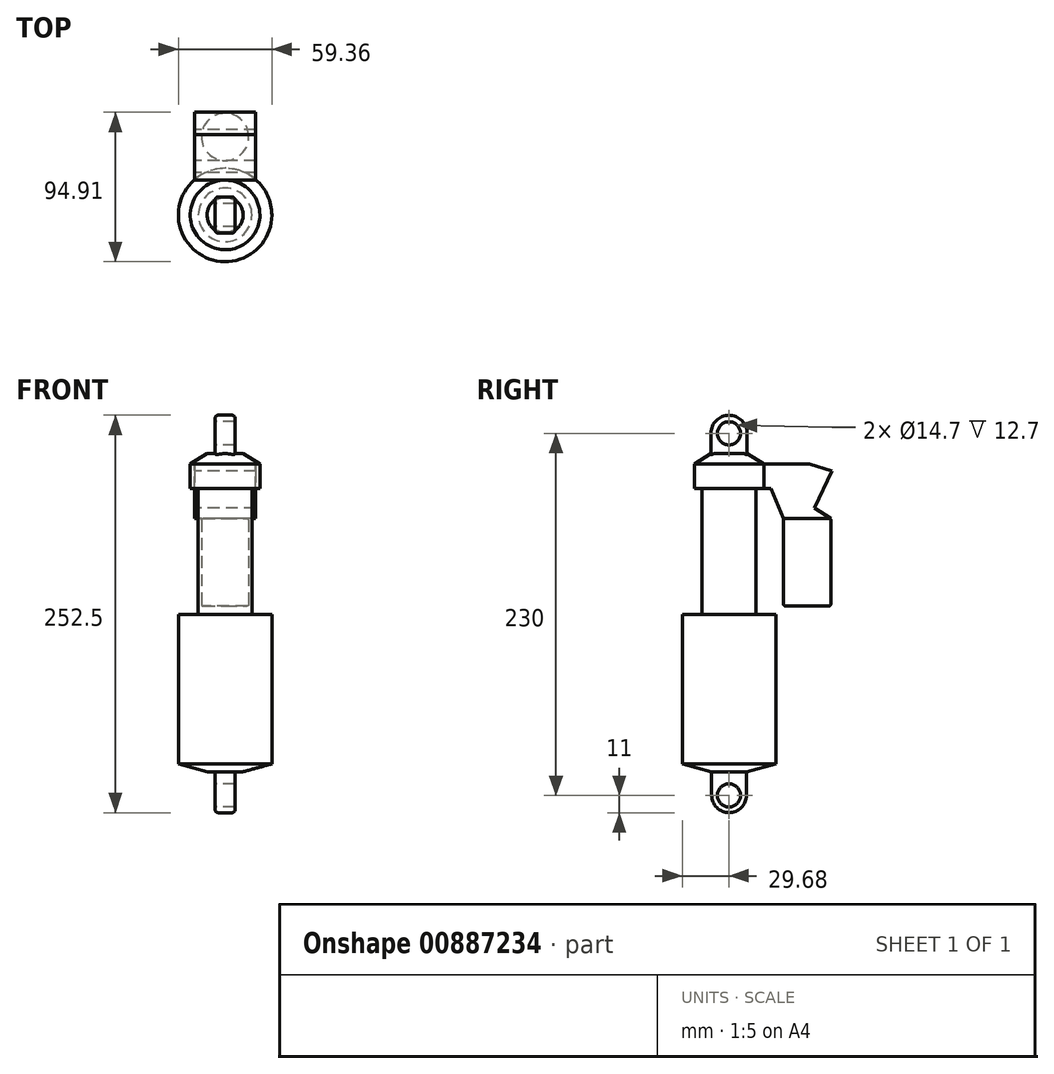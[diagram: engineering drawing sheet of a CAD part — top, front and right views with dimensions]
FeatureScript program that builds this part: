
annotation { "Feature Type Name" : "Feature", "Feature Type Description" : "" }
export const myFeature = defineFeature(function(context is Context, id is Id, definition is map)
    precondition{}
    {
        {
            var Q0;
            Q0=qCreatedBy(makeId("Right.planeOp"),FACE);
            var sketch = newSketch(context, id + "F0", { "sketchPlane" : qUnion([Q0])});
            skCircle(sketch, "E0", {"center": v(0, 0) * mm, "radius": 7.35 * mm});
            skCircle(sketch, "E1", {"center": v(0, 0) * mm, "radius": 11 * mm});
            skCircle(sketch, "E2", {"center": v(0, 230) * mm, "radius": 7.35 * mm});
            skCircle(sketch, "E3", {"center": v(0, 230) * mm, "radius": 11.5 * mm});
            skLineSegment(sketch, "E4.bottom", {"start": v(29.67, 20) * mm, "end": v(-29.68, 20) * mm});
            skLineSegment(sketch, "E4.top", {"start": v(29.67, 115) * mm, "end": v(-29.68, 115) * mm});
            skLineSegment(sketch, "E4.left", {"start": v(29.67, 20) * mm, "end": v(29.67, 115) * mm});
            skLineSegment(sketch, "E4.right", {"start": v(-29.68, 20) * mm, "end": v(-29.68, 115) * mm});
            skPoint(sketch, "E4.middle", {"position": v(0, 67.5) * mm});
            skLineSegment(sketch, "E5.bottom", {"start": v(17, 115) * mm, "end": v(-17, 115) * mm});
            skLineSegment(sketch, "E5.top", {"start": v(17, 195) * mm, "end": v(-17, 195) * mm});
            skLineSegment(sketch, "E5.left", {"start": v(17, 115) * mm, "end": v(17, 195) * mm});
            skLineSegment(sketch, "E5.right", {"start": v(-17, 115) * mm, "end": v(-17, 195) * mm});
            skPoint(sketch, "E5.middle", {"position": v(0, 155) * mm});
            skLineSegment(sketch, "E6.bottom", {"start": v(22.1, 195) * mm, "end": v(-22.1, 195) * mm});
            skLineSegment(sketch, "E6.top", {"start": v(22.1, 210.48) * mm, "end": v(-22.1, 210.48) * mm});
            skLineSegment(sketch, "E6.left", {"start": v(22.1, 195) * mm, "end": v(22.1, 210.48) * mm});
            skLineSegment(sketch, "E6.right", {"start": v(-22.1, 195) * mm, "end": v(-22.1, 210.48) * mm});
            skPoint(sketch, "E6.middle", {"position": v(0, 202.74) * mm});
            skPoint(sketch, "E6.cornerSnap0", {"position": v(0, 195) * mm});
            skLineSegment(sketch, "E7.bottom", {"start": v(34.6, 120.35) * mm, "end": v(64.6, 120.35) * mm});
            skLineSegment(sketch, "E7.top", {"start": v(34.6, 175.94) * mm, "end": v(64.6, 175.94) * mm});
            skLineSegment(sketch, "E7.left", {"start": v(34.6, 120.35) * mm, "end": v(34.6, 175.94) * mm});
            skLineSegment(sketch, "E7.right", {"start": v(64.6, 120.35) * mm, "end": v(64.6, 175.94) * mm});
            skLineSegment(sketch, "E8", {"start": v(0, 230) * mm, "end": v(0, 0) * mm});
            skLineSegment(sketch, "E9", {"start": v(-11.5, 230) * mm, "end": v(-11.46, 210.48) * mm});
            skLineSegment(sketch, "E10.MirrorCS", {"start": v(11.5, 230) * mm, "end": v(11.46, 210.48) * mm});
            skLineSegment(sketch, "E11", {"start": v(22.1, 210.48) * mm, "end": v(51.15, 210.48) * mm});
            skLineSegment(sketch, "E12", {"start": v(51.15, 210.48) * mm, "end": v(65.23, 206.1) * mm});
            skLineSegment(sketch, "E13", {"start": v(65.23, 206.1) * mm, "end": v(54.26, 182.55) * mm});
            skLineSegment(sketch, "E14", {"start": v(54.26, 182.55) * mm, "end": v(64.6, 175.94) * mm});
            skLineSegment(sketch, "E15", {"start": v(34.6, 175.94) * mm, "end": v(32.36, 181.41) * mm});
            skLineSegment(sketch, "E16", {"start": v(32.36, 181.41) * mm, "end": v(26.78, 195) * mm});
            skLineSegment(sketch, "E17", {"start": v(26.78, 195) * mm, "end": v(22.1, 195) * mm});
            skLineSegment(sketch, "E18", {"start": v(11.47, 217.1) * mm, "end": v(51.15, 210.48) * mm});
            skLineSegment(sketch, "E19", {"start": v(-22.1, 210.48) * mm, "end": v(-11.47, 217.1) * mm});
            skLineSegment(sketch, "E20", {"start": v(-29.68, 20) * mm, "end": v(-11, 14.91) * mm});
            skLineSegment(sketch, "E21", {"start": v(-11, 0) * mm, "end": v(-11, 14.91) * mm});
            skLineSegment(sketch, "E22.MirrorCS", {"start": v(11, 0) * mm, "end": v(11, 14.91) * mm});
            skLineSegment(sketch, "E23.MirrorCS", {"start": v(29.68, 20) * mm, "end": v(11, 14.91) * mm});
            skLineSegment(sketch, "E24", {"start": v(49.6, 120.35) * mm, "end": v(49.6, 175.94) * mm});
            skLineSegment(sketch, "E25", {"start": v(-11.47, 217.1) * mm, "end": v(11.47, 217.1) * mm});
            skLineSegment(sketch, "E26", {"start": v(-11, 14.91) * mm, "end": v(11, 14.91) * mm});
            skSolve(sketch);
        }
        {
            var Q0;
            {var subQ5=sQuery(id+"F0.wireOp",EDGE,"E4.right");Q0=makeQuery(id+"F0.imprint","IMPRINT",FACE,{"disambiguationData":[TD([[makeQuery(id+"F0.imprint","IMPRINT",EDGE,{"derivedFrom":subQ5}),-1.0]])]});}
            var Q1;
            Q1=sQuery(id+"F0.wireOp",EDGE,"E8");
            revolve(context, id + "F1", {"surfaceOperationType" : NewSurfaceOperationType.NEW, "entities" : qUnion([Q0]), "axis" : qUnion([Q1]), "revolveType" : RevolveType.FULL});
        }
        {
            var Q0;
            {var subQ0=sQuery(id+"F0.wireOp",EDGE,"E5.right");Q0=makeQuery(id+"F0.imprint","IMPRINT",FACE,{"disambiguationData":[TD([[makeQuery(id+"F0.imprint","IMPRINT",EDGE,{"derivedFrom":subQ0}),-1.0]])]});}
            var Q1;
            Q1=sQuery(id+"F0.wireOp",EDGE,"E8");
            revolve(context, id + "F2", {"operationType" : NewBodyOperationType.ADD, "surfaceOperationType" : NewSurfaceOperationType.NEW, "entities" : qUnion([Q0]), "axis" : qUnion([Q1]), "revolveType" : RevolveType.FULL});
        }
        {
            var Q0;
            {var subQ0=sQuery(id+"F0.wireOp",EDGE,"E7.left");Q0=makeQuery(id+"F0.imprint","IMPRINT",FACE,{"disambiguationData":[TD([[makeQuery(id+"F0.imprint","IMPRINT",EDGE,{"derivedFrom":subQ0}),-1.0]])]});}
            var Q1;
            Q1=sQuery(id+"F0.wireOp",EDGE,"E24");
            revolve(context, id + "F3", {"surfaceOperationType" : NewSurfaceOperationType.NEW, "entities" : qUnion([Q0]), "axis" : qUnion([Q1]), "revolveType" : RevolveType.FULL});
        }
        {
            var Q0;
            {var subQ0=sQuery(id+"F0.wireOp",EDGE,"E19");Q0=makeQuery(id+"F0.imprint","IMPRINT",FACE,{"disambiguationData":[TD([[makeQuery(id+"F0.imprint","IMPRINT",EDGE,{"derivedFrom":subQ0}),-1.0]])]});}
            var Q1;
            {var subQ0=sQuery(id+"F0.wireOp",EDGE,"E9");var subQ1=sQuery(id+"F0.wireOp",EDGE,"E6.top");var subQ2=makeQuery(id+"F0.imprint","INTERSECT",VERTEX,{"derivedFrom":[subQ1,subQ0]});Q1=makeQuery(id+"F0.imprint","IMPRINT",FACE,{"disambiguationData":[TD([[makeQuery(id+"F0.imprint","IMPRINT",EDGE,{"disambiguationData":[TD([[subQ2,1.0]])],"derivedFrom":subQ1}),-1.0]])]});}
            var Q2;
            {var subQ6=sQuery(id+"F0.wireOp",EDGE,"E6.right");Q2=makeQuery(id+"F0.imprint","IMPRINT",FACE,{"disambiguationData":[TD([[makeQuery(id+"F0.imprint","IMPRINT",EDGE,{"derivedFrom":subQ6}),-1.0]])]});}
            var Q3;
            {var subQ0=sQuery(id+"F0.wireOp",EDGE,"E20");Q3=makeQuery(id+"F0.imprint","IMPRINT",FACE,{"disambiguationData":[TD([[makeQuery(id+"F0.imprint","IMPRINT",EDGE,{"derivedFrom":subQ0}),1.0]])]});}
            var Q4;
            Q4=sQuery(id+"F0.wireOp",EDGE,"E8");
            revolve(context, id + "F4", {"operationType" : NewBodyOperationType.ADD, "surfaceOperationType" : NewSurfaceOperationType.NEW, "entities" : qUnion([Q0, Q1, Q2, Q3]), "axis" : qUnion([Q4]), "revolveType" : RevolveType.FULL});
        }
        {
            var Q0;
            Q0=makeQuery(id+"F0.imprint","IMPRINT",FACE,{"disambiguationData":[TD([[makeQuery(id+"F0.imprint","IMPRINT",EDGE,{"derivedFrom":sQuery(id+"F0.wireOp",EDGE,"E2")}),-1.0]])]});
            var Q1;
            {var subQ0=sQuery(id+"F0.wireOp",EDGE,"E9");var subQ1=sQuery(id+"F0.wireOp",EDGE,"E3");var subQ2=makeQuery(id+"F0.imprint","INTERSECT",VERTEX,{"derivedFrom":[subQ1,subQ0]});Q1=makeQuery(id+"F0.imprint","IMPRINT",FACE,{"disambiguationData":[TD([[makeQuery(id+"F0.imprint","IMPRINT",EDGE,{"disambiguationData":[TD([[subQ2,-1.0]])],"derivedFrom":subQ1}),-1.0]])]});}
            var Q2;
            {var subQ0=sQuery(id+"F0.wireOp",EDGE,"E10.MirrorCS");var subQ1=sQuery(id+"F0.wireOp",EDGE,"E3");var subQ2=makeQuery(id+"F0.imprint","INTERSECT",VERTEX,{"derivedFrom":[subQ1,subQ0]});Q2=makeQuery(id+"F0.imprint","IMPRINT",FACE,{"disambiguationData":[TD([[makeQuery(id+"F0.imprint","IMPRINT",EDGE,{"disambiguationData":[TD([[subQ2,1.0]])],"derivedFrom":subQ1}),-1.0]])]});}
            var Q3;
            {var subQ0=sQuery(id+"F0.wireOp",EDGE,"E22.MirrorCS");Q3=makeQuery(id+"F0.imprint","IMPRINT",FACE,{"disambiguationData":[TD([[makeQuery(id+"F0.imprint","IMPRINT",EDGE,{"derivedFrom":subQ0}),1.0]])]});}
            var Q4;
            {var subQ0=sQuery(id+"F0.wireOp",EDGE,"E21");Q4=makeQuery(id+"F0.imprint","IMPRINT",FACE,{"disambiguationData":[TD([[makeQuery(id+"F0.imprint","IMPRINT",EDGE,{"derivedFrom":subQ0}),-1.0]])]});}
            var Q5;
            Q5=makeQuery(id+"F0.imprint","IMPRINT",FACE,{"disambiguationData":[TD([[makeQuery(id+"F0.imprint","IMPRINT",EDGE,{"derivedFrom":sQuery(id+"F0.wireOp",EDGE,"E0")}),-1.0]])]});
            extrude(context, id + "F5", {"entities" : qUnion([Q0, Q1, Q2, Q3, Q4, Q5]), "operationType" : NewBodyOperationType.ADD, "depth" : 12.7 * mm, "offsetDistance" : 25 * mm, "symmetric" : true});
        }
        {
            var Q0;
            Q0=makeQuery(id+"F0.imprint","IMPRINT",FACE,{"disambiguationData":[TD([[makeQuery(id+"F0.imprint","IMPRINT",EDGE,{"derivedFrom":sQuery(id+"F0.wireOp",EDGE,"E6.left")}),-1.0]])]});
            extrude(context, id + "F6", {"entities" : qUnion([Q0]), "depth" : 39 * mm, "offsetDistance" : 25 * mm, "symmetric" : true});
        }
        {
            var Q0;
            Q0=makeQuery(id+"F5.opExtrude","CAP_EDGE",EDGE,{"disambiguationData":[OSD([sQuery(id+"F0.wireOp",EDGE,"E3")])],"isStart":false});
            var Q1;
            Q1=makeQuery(id+"F5.opExtrude","CAP_EDGE",EDGE,{"disambiguationData":[OSD([sQuery(id+"F0.wireOp",EDGE,"E9")])],"isStart":false});
            var Q2;
            Q2=makeQuery(id+"F5.opExtrude","CAP_EDGE",EDGE,{"disambiguationData":[OSD([sQuery(id+"F0.wireOp",EDGE,"E10.MirrorCS")])],"isStart":false});
            var Q3;
            Q3=makeQuery(id+"F5.opExtrude","CAP_EDGE",EDGE,{"disambiguationData":[OSD([sQuery(id+"F0.wireOp",EDGE,"E9")])],"isStart":true});
            var Q4;
            Q4=makeQuery(id+"F5.opExtrude","CAP_EDGE",EDGE,{"disambiguationData":[OSD([sQuery(id+"F0.wireOp",EDGE,"E3")])],"isStart":true});
            var Q5;
            Q5=makeQuery(id+"F5.opExtrude","CAP_EDGE",EDGE,{"disambiguationData":[OSD([sQuery(id+"F0.wireOp",EDGE,"E10.MirrorCS")])],"isStart":true});
            var Q6;
            Q6=makeQuery(id+"F5.opExtrude","CAP_EDGE",EDGE,{"disambiguationData":[OSD([sQuery(id+"F0.wireOp",EDGE,"E1")])],"isStart":true});
            var Q7;
            Q7=makeQuery(id+"F5.opExtrude","CAP_EDGE",EDGE,{"disambiguationData":[OSD([sQuery(id+"F0.wireOp",EDGE,"E21")])],"isStart":true});
            var Q8;
            Q8=makeQuery(id+"F5.opExtrude","CAP_EDGE",EDGE,{"disambiguationData":[OSD([sQuery(id+"F0.wireOp",EDGE,"E22.MirrorCS")])],"isStart":false});
            var Q9;
            Q9=makeQuery(id+"F5.opExtrude","CAP_EDGE",EDGE,{"disambiguationData":[OSD([sQuery(id+"F0.wireOp",EDGE,"E1")])],"isStart":false});
            var Q10;
            Q10=makeQuery(id+"F5.opExtrude","CAP_EDGE",EDGE,{"disambiguationData":[OSD([sQuery(id+"F0.wireOp",EDGE,"E21")])],"isStart":false});
            fillet(context, id + "F7", {"entities" : qUnion([Q0, Q1, Q2, Q3, Q4, Q5, Q6, Q7, Q8, Q9, Q10]), "radius" : 2 * mm, "tangentPropagation" : true, "allowEdgeOverflow" : false});
        }
        {
            var Q0;
            {var subQ0=sQuery(id+"F0.wireOp",EDGE,"E10.MirrorCS");var subQ1=sQuery(id+"F0.wireOp",EDGE,"E25");var subQ2=makeQuery(id+"F5.opExtrude","SWEPT_FACE",FACE,{"disambiguationData":[OSD([subQ1])]});Q0=makeQuery(id+"F5.boolean.opBoolean","SPLIT",FACE,{"disambiguationData":[TD([makeQuery(id+"F4.opRevolve","SWEPT_FACE",FACE,{"disambiguationData":[OSD([sQuery(id+"F0.wireOp",EDGE,"E19")])]}),makeQuery(id+"F4.opRevolve","SWEPT_FACE",FACE,{"disambiguationData":[OSD([subQ1])]}),makeQuery(id+"F5.opExtrude","CAP_FACE",FACE,{"disambiguationData":[OSD([sQuery(id+"F0.wireOp",EDGE,"E2"),sQuery(id+"F0.wireOp",EDGE,"E3"),sQuery(id+"F0.wireOp",EDGE,"E9"),subQ0,subQ1])],"isStart":true}),makeQuery(id+"F5.opExtrude","SWEPT_FACE",FACE,{"disambiguationData":[OSD([subQ0])]}),subQ2])],"derivedFrom":subQ2});}
            var Q1;
            {var subQ0=sQuery(id+"F0.wireOp",EDGE,"E10.MirrorCS");var subQ1=sQuery(id+"F0.wireOp",EDGE,"E25");var subQ2=makeQuery(id+"F5.opExtrude","SWEPT_FACE",FACE,{"disambiguationData":[OSD([subQ1])]});Q1=makeQuery(id+"F5.boolean.opBoolean","SPLIT",FACE,{"disambiguationData":[TD([makeQuery(id+"F4.opRevolve","SWEPT_FACE",FACE,{"disambiguationData":[OSD([sQuery(id+"F0.wireOp",EDGE,"E19")])]}),makeQuery(id+"F4.opRevolve","SWEPT_FACE",FACE,{"disambiguationData":[OSD([subQ1])]}),makeQuery(id+"F5.opExtrude","CAP_FACE",FACE,{"disambiguationData":[OSD([sQuery(id+"F0.wireOp",EDGE,"E2"),sQuery(id+"F0.wireOp",EDGE,"E3"),sQuery(id+"F0.wireOp",EDGE,"E9"),subQ0,subQ1])],"isStart":false}),makeQuery(id+"F5.opExtrude","SWEPT_FACE",FACE,{"disambiguationData":[OSD([subQ0])]}),subQ2])],"derivedFrom":subQ2});}
            var Q2;
            {var subQ0=sQuery(id+"F0.wireOp",EDGE,"E9");var subQ1=sQuery(id+"F0.wireOp",EDGE,"E25");var subQ2=makeQuery(id+"F5.opExtrude","SWEPT_FACE",FACE,{"disambiguationData":[OSD([subQ1])]});Q2=makeQuery(id+"F5.boolean.opBoolean","SPLIT",FACE,{"disambiguationData":[TD([makeQuery(id+"F4.opRevolve","SWEPT_FACE",FACE,{"disambiguationData":[OSD([sQuery(id+"F0.wireOp",EDGE,"E19")])]}),makeQuery(id+"F4.opRevolve","SWEPT_FACE",FACE,{"disambiguationData":[OSD([subQ1])]}),makeQuery(id+"F5.opExtrude","CAP_FACE",FACE,{"disambiguationData":[OSD([sQuery(id+"F0.wireOp",EDGE,"E2"),sQuery(id+"F0.wireOp",EDGE,"E3"),subQ0,sQuery(id+"F0.wireOp",EDGE,"E10.MirrorCS"),subQ1])],"isStart":false}),makeQuery(id+"F5.opExtrude","SWEPT_FACE",FACE,{"disambiguationData":[OSD([subQ0])]}),subQ2])],"derivedFrom":subQ2});}
            var Q3;
            {var subQ0=sQuery(id+"F0.wireOp",EDGE,"E25");var subQ1=sQuery(id+"F0.wireOp",EDGE,"E9");var subQ2=makeQuery(id+"F5.opExtrude","SWEPT_FACE",FACE,{"disambiguationData":[OSD([subQ0])]});Q3=makeQuery(id+"F5.boolean.opBoolean","SPLIT",FACE,{"disambiguationData":[TD([makeQuery(id+"F4.opRevolve","SWEPT_FACE",FACE,{"disambiguationData":[OSD([sQuery(id+"F0.wireOp",EDGE,"E19")])]}),makeQuery(id+"F4.opRevolve","SWEPT_FACE",FACE,{"disambiguationData":[OSD([subQ0])]}),makeQuery(id+"F5.opExtrude","CAP_FACE",FACE,{"disambiguationData":[OSD([sQuery(id+"F0.wireOp",EDGE,"E2"),sQuery(id+"F0.wireOp",EDGE,"E3"),subQ1,sQuery(id+"F0.wireOp",EDGE,"E10.MirrorCS"),subQ0])],"isStart":true}),makeQuery(id+"F5.opExtrude","SWEPT_FACE",FACE,{"disambiguationData":[OSD([subQ1])]}),subQ2])],"derivedFrom":subQ2});}
            extrude(context, id + "F8", {"entities" : qUnion([Q0, Q1, Q2, Q3]), "operationType" : NewBodyOperationType.ADD, "depth" : 1 * mm, "offsetDistance" : 25 * mm});
        }
        {
            var Q0;
            {var subQ0=sQuery(id+"F0.wireOp",EDGE,"E25");Q0=makeQuery(id+"F5.boolean.opBoolean","SPLIT",EDGE,{"disambiguationData":[topologyDisambiguationEdgeConnected([makeQuery(id+"F4.opRevolve","SWEPT_FACE",FACE,{"disambiguationData":[OSD([subQ0])]}),makeQuery(id+"F5.opExtrude","CAP_FACE",FACE,{"disambiguationData":[OSD([sQuery(id+"F0.wireOp",EDGE,"E2"),sQuery(id+"F0.wireOp",EDGE,"E3"),sQuery(id+"F0.wireOp",EDGE,"E9"),sQuery(id+"F0.wireOp",EDGE,"E10.MirrorCS"),subQ0])],"isStart":true})])],"derivedFrom":makeQuery(id+"F5.opExtrude","CAP_EDGE",EDGE,{"disambiguationData":[OSD([subQ0])],"isStart":true})});}
            var Q1;
            {var subQ0=sQuery(id+"F0.wireOp",EDGE,"E25");Q1=makeQuery(id+"F5.boolean.opBoolean","SPLIT",EDGE,{"disambiguationData":[topologyDisambiguationEdgeConnected([makeQuery(id+"F4.opRevolve","SWEPT_FACE",FACE,{"disambiguationData":[OSD([subQ0])]}),makeQuery(id+"F5.opExtrude","CAP_FACE",FACE,{"disambiguationData":[OSD([sQuery(id+"F0.wireOp",EDGE,"E2"),sQuery(id+"F0.wireOp",EDGE,"E3"),sQuery(id+"F0.wireOp",EDGE,"E9"),sQuery(id+"F0.wireOp",EDGE,"E10.MirrorCS"),subQ0])],"isStart":false})])],"derivedFrom":makeQuery(id+"F5.opExtrude","CAP_EDGE",EDGE,{"disambiguationData":[OSD([subQ0])],"isStart":false})});}
            var Q2;
            {var subQ0=sQuery(id+"F0.wireOp",EDGE,"E26");Q2=makeQuery(id+"F5.boolean.opBoolean","SPLIT",EDGE,{"disambiguationData":[topologyDisambiguationEdgeConnected([makeQuery(id+"F4.opRevolve","SWEPT_FACE",FACE,{"disambiguationData":[OSD([subQ0])]}),makeQuery(id+"F5.opExtrude","CAP_FACE",FACE,{"disambiguationData":[OSD([sQuery(id+"F0.wireOp",EDGE,"E0"),sQuery(id+"F0.wireOp",EDGE,"E1"),sQuery(id+"F0.wireOp",EDGE,"E21"),sQuery(id+"F0.wireOp",EDGE,"E22.MirrorCS"),subQ0])],"isStart":true})])],"derivedFrom":makeQuery(id+"F5.opExtrude","CAP_EDGE",EDGE,{"disambiguationData":[OSD([subQ0])],"isStart":true})});}
            var Q3;
            {var subQ0=sQuery(id+"F0.wireOp",EDGE,"E26");Q3=makeQuery(id+"F5.boolean.opBoolean","SPLIT",EDGE,{"disambiguationData":[topologyDisambiguationEdgeConnected([makeQuery(id+"F4.opRevolve","SWEPT_FACE",FACE,{"disambiguationData":[OSD([subQ0])]}),makeQuery(id+"F5.opExtrude","CAP_FACE",FACE,{"disambiguationData":[OSD([sQuery(id+"F0.wireOp",EDGE,"E0"),sQuery(id+"F0.wireOp",EDGE,"E1"),sQuery(id+"F0.wireOp",EDGE,"E21"),sQuery(id+"F0.wireOp",EDGE,"E22.MirrorCS"),subQ0])],"isStart":false})])],"derivedFrom":makeQuery(id+"F5.opExtrude","CAP_EDGE",EDGE,{"disambiguationData":[OSD([subQ0])],"isStart":false})});}
            var Q4;
            {var subQ0=sQuery(id+"F0.wireOp",EDGE,"E20");var subQ1=sQuery(id+"F0.wireOp",EDGE,"E4.right");var subQ2=sQuery(id+"F0.wireOp",EDGE,"E4.bottom");Q4=makeQuery(id+"F4.boolean.opBoolean","MERGE",EDGE,{"derivedFrom":[makeQuery(id+"F1.opRevolve","SWEPT_EDGE",EDGE,{"disambiguationData":[OSD([subQ2,subQ1,subQ0])]}),makeQuery(id+"F4.opRevolve","SWEPT_EDGE",EDGE,{"disambiguationData":[OSD([subQ2,subQ1,subQ0])]})]});}
            var Q5;
            Q5=makeQuery(id+"F1.opRevolve","SWEPT_EDGE",EDGE,{"disambiguationData":[OSD([sQuery(id+"F0.wireOp",EDGE,"E4.top"),sQuery(id+"F0.wireOp",EDGE,"E4.right")])]});
            var Q6;
            Q6=makeQuery(id+"F2.opRevolve","SWEPT_EDGE",EDGE,{"disambiguationData":[OSD([sQuery(id+"F0.wireOp",EDGE,"E4.top"),sQuery(id+"F0.wireOp",EDGE,"E5.bottom"),sQuery(id+"F0.wireOp",EDGE,"E5.right")])]});
            var Q7;
            Q7=makeQuery(id+"F3.opRevolve","SWEPT_EDGE",EDGE,{"disambiguationData":[OSD([sQuery(id+"F0.wireOp",EDGE,"E7.bottom"),sQuery(id+"F0.wireOp",EDGE,"E7.left")])]});
            var Q8;
            Q8=makeQuery(id+"F4.opRevolve","SWEPT_EDGE",EDGE,{"disambiguationData":[OSD([sQuery(id+"F0.wireOp",EDGE,"E6.top"),sQuery(id+"F0.wireOp",EDGE,"E6.right"),sQuery(id+"F0.wireOp",EDGE,"E19")])]});
            var Q9;
            Q9=makeQuery(id+"F4.opRevolve","SWEPT_EDGE",EDGE,{"disambiguationData":[OSD([sQuery(id+"F0.wireOp",EDGE,"E6.bottom"),sQuery(id+"F0.wireOp",EDGE,"E6.right")])]});
            var Q10;
            Q10=makeQuery(id+"F3.opRevolve","SWEPT_EDGE",EDGE,{"disambiguationData":[OSD([sQuery(id+"F0.wireOp",EDGE,"E7.top"),sQuery(id+"F0.wireOp",EDGE,"E7.left"),sQuery(id+"F0.wireOp",EDGE,"E15")])]});
            fillet(context, id + "F9", {"entities" : qUnion([Q0, Q1, Q2, Q3, Q4, Q5, Q6, Q7, Q8, Q9, Q10]), "radius" : 1 * mm, "tangentPropagation" : true, "allowEdgeOverflow" : false});
        }
    });
